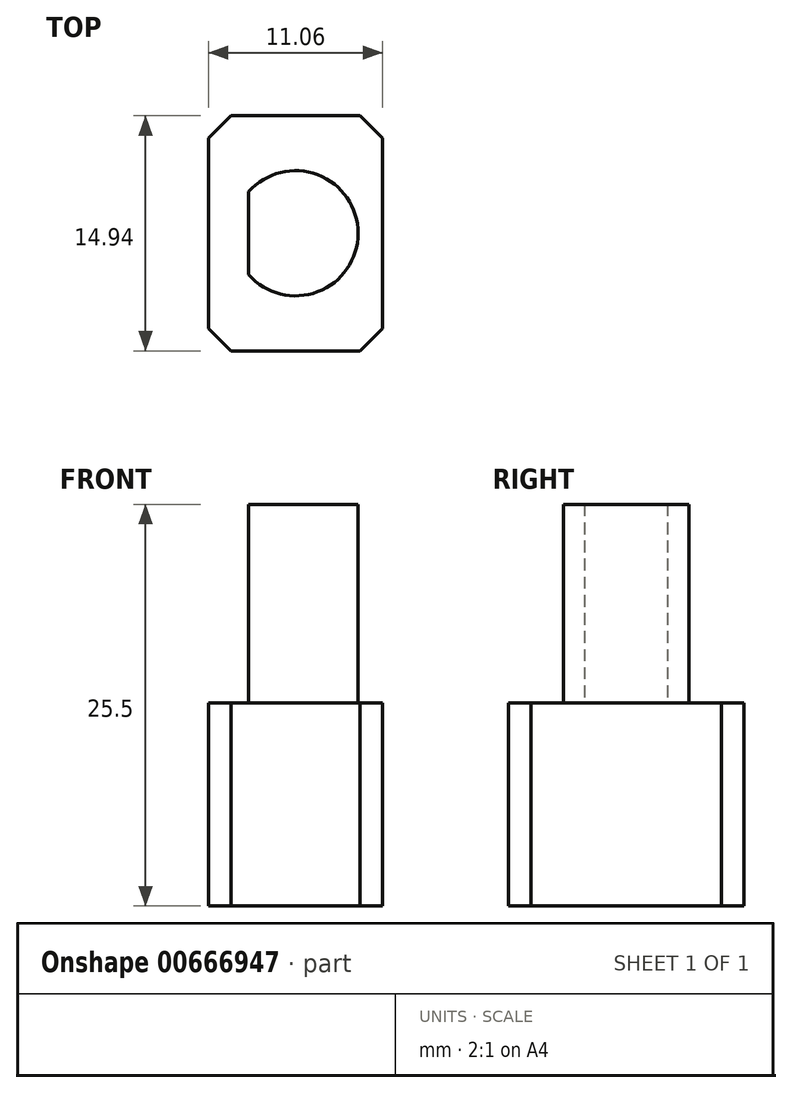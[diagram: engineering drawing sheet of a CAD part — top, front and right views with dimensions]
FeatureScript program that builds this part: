
annotation { "Feature Type Name" : "Feature", "Feature Type Description" : "" }
export const myFeature = defineFeature(function(context is Context, id is Id, definition is map)
    precondition{}
    {
        {
            var Q0;
            Q0=qCreatedBy(makeId("Top.planeOp"),FACE);
            var sketch = newSketch(context, id + "F0", { "sketchPlane" : qUnion([Q0])});
            skCircle(sketch, "E0", {"center": v(0, 0) * mm, "radius": 3.98 * mm});
            skPoint(sketch, "E1", {"position": v(-3.98, 0) * mm});
            skLineSegment(sketch, "E2", {"start": v(-2.98, 2.64) * mm, "end": v(-2.97, -2.64) * mm});
            skLineSegment(sketch, "E3", {"start": v(-2.98, 0) * mm, "end": v(3.98, 0) * mm});
            skSolve(sketch);
        }
        {
            var Q0;
            Q0 = qSketchRegion(id + "F0", true);
            extrude(context, id + "F1", {"entities" : qUnion([Q0]), "depth" : 12.6 * mm, "offsetDistance" : 25 * mm});
        }
        {
            var Q0;
            {var subQ0=sQuery(id+"F0.wireOp",EDGE,"E2");Q0=makeQuery(id+"F0.imprint","IMPRINT",FACE,{"disambiguationData":[TD([[makeQuery(id+"F0.imprint","IMPRINT",EDGE,{"derivedFrom":subQ0}),-1.0]])]});}
            extrude(context, id + "F2", {"entities" : qUnion([Q0]), "operationType" : NewBodyOperationType.REMOVE, "depth" : 12.6 * mm, "offsetDistance" : 25 * mm});
        }
        {
            var Q0;
            {var subQ0=sQuery(id+"F0.wireOp",EDGE,"E2");Q0=makeQuery(id+"F0.imprint","IMPRINT",FACE,{"disambiguationData":[TD([[makeQuery(id+"F0.imprint","IMPRINT",EDGE,{"derivedFrom":subQ0}),1.0]])]});}
            var sketch = newSketch(context, id + "F3", { "sketchPlane" : qUnion([Q0])});
            skLineSegment(sketch, "E4.bottom", {"start": v(4.11, 7.47) * mm, "end": v(-4.11, 7.47) * mm});
            skLineSegment(sketch, "E4.top", {"start": v(4.11, -7.48) * mm, "end": v(-4.11, -7.48) * mm});
            skLineSegment(sketch, "E4.left", {"start": v(5.53, 6.06) * mm, "end": v(5.53, -6.06) * mm});
            skLineSegment(sketch, "E4.right", {"start": v(-5.53, 6.06) * mm, "end": v(-5.52, -6.06) * mm});
            skPoint(sketch, "E4.middle", {"position": v(0, 0) * mm});
            skPoint(sketch, "E5", {"position": v(-5.52, -6.06) * mm});
            skPoint(sketch, "E6", {"position": v(4.11, -7.48) * mm});
            skPoint(sketch, "E7", {"position": v(5.53, -6.06) * mm});
            skPoint(sketch, "E8", {"position": v(-5.53, 6.06) * mm});
            skPoint(sketch, "E9", {"position": v(-4.11, 7.47) * mm});
            skPoint(sketch, "E10", {"position": v(4.11, 7.48) * mm});
            skPoint(sketch, "E11", {"position": v(5.53, 6.06) * mm});
            skPoint(sketch, "E12", {"position": v(-5.53, 0) * mm});
            skPoint(sketch, "E13", {"position": v(5.53, 0) * mm});
            skPoint(sketch, "E14", {"position": v(0, -7.48) * mm});
            skPoint(sketch, "E15", {"position": v(0, 7.47) * mm});
            skLineSegment(sketch, "E16", {"start": v(-4.11, 7.47) * mm, "end": v(-5.53, 6.06) * mm});
            skPoint(sketch, "E17", {"position": v(-4.11, -7.48) * mm});
            skLineSegment(sketch, "E18", {"start": v(-4.11, -7.48) * mm, "end": v(-5.52, -6.06) * mm});
            skLineSegment(sketch, "E19", {"start": v(4.11, -7.48) * mm, "end": v(5.53, -6.06) * mm});
            skLineSegment(sketch, "E20", {"start": v(5.53, 6.06) * mm, "end": v(4.11, 7.48) * mm});
            skPoint(sketch, "E21.orphan", {"position": v(-5.52, -7.48) * mm});
            skPoint(sketch, "E22.orphan", {"position": v(5.53, -7.48) * mm});
            skPoint(sketch, "E23.orphan", {"position": v(5.52, 7.47) * mm});
            skPoint(sketch, "E24.orphan", {"position": v(-5.53, 7.47) * mm});
            skSolve(sketch);
        }
        {
            var Q0;
            Q0 = qSketchRegion(id + "F3", true);
            extrude(context, id + "F4", {"entities" : qUnion([Q0]), "operationType" : NewBodyOperationType.ADD, "oppositeDirection" : true, "depth" : 12.9 * mm, "offsetDistance" : 25 * mm});
        }
    });
